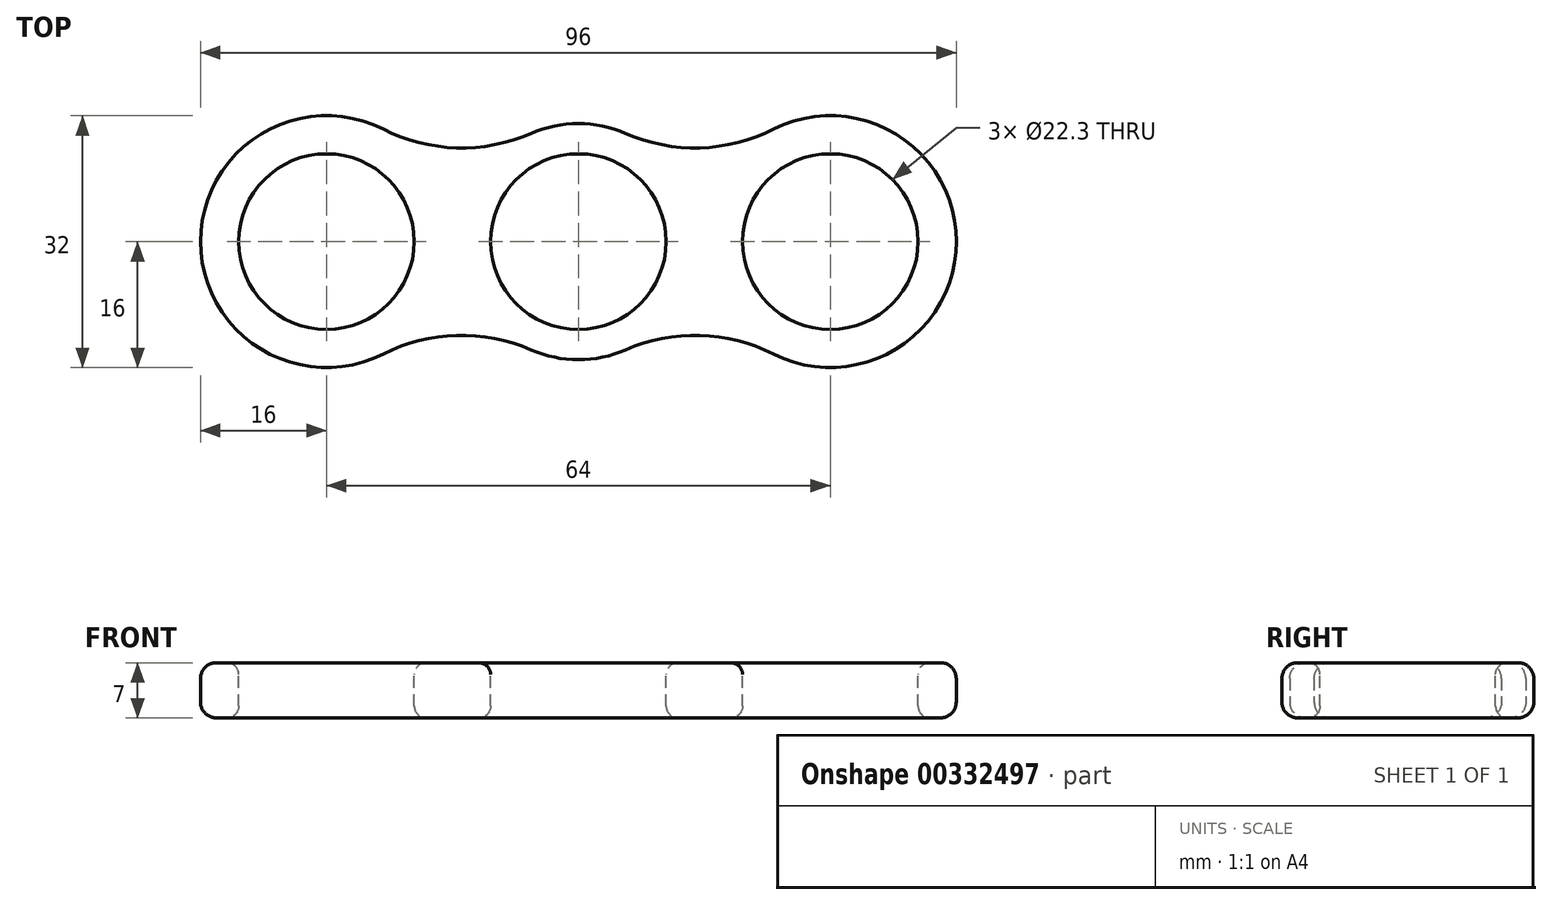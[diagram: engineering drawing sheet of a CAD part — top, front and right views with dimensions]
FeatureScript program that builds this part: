
annotation { "Feature Type Name" : "Feature", "Feature Type Description" : "" }
export const myFeature = defineFeature(function(context is Context, id is Id, definition is map)
    precondition{}
    {
        {
            var Q0;
            Q0=qCreatedBy(makeId("Top.planeOp"),FACE);
            var sketch = newSketch(context, id + "F0", { "sketchPlane" : qUnion([Q0])});
            skArc(sketch, "E0", {"start": v(-6.01, -13.74) * mm, "mid": v(0, -15) * mm, "end": v(6.01, -13.74) * mm});
            skArc(sketch, "E1", {"start": v(-24.77, 14.27) * mm, "mid": v(-45.74, 8.2) * mm, "end": v(-41.14, -13.13) * mm});
            skArc(sketch, "E2", {"start": v(24.77, -14.27) * mm, "mid": v(33.11, -15.96) * mm, "end": v(41.14, -13.13) * mm});
            skArc(sketch, "E3", {"start": v(-24.77, 14.27) * mm, "mid": v(-15.45, 11.9) * mm, "end": v(-6.01, 13.74) * mm});
            skArc(sketch, "E4", {"start": v(-6.01, -13.74) * mm, "mid": v(-15.45, -11.9) * mm, "end": v(-24.77, -14.27) * mm});
            skArc(sketch, "E5", {"start": v(6.01, 13.74) * mm, "mid": v(15.45, 11.9) * mm, "end": v(24.77, 14.27) * mm});
            skArc(sketch, "E6", {"start": v(24.77, -14.27) * mm, "mid": v(15.45, -11.9) * mm, "end": v(6.01, -13.74) * mm});
            skArc(sketch, "E7.trimOffspring", {"start": v(6.01, 13.74) * mm, "mid": v(0, 15) * mm, "end": v(-6.01, 13.74) * mm});
            skArc(sketch, "E8.trimOffspring", {"start": v(-41.14, -13.13) * mm, "mid": v(-33.11, -15.96) * mm, "end": v(-24.77, -14.27) * mm});
            skArc(sketch, "E9.trimOffspring", {"start": v(41.14, -13.13) * mm, "mid": v(45.74, 8.2) * mm, "end": v(24.77, 14.27) * mm});
            skSolve(sketch);
        }
        {
            var Q0;
            Q0 = qSketchRegion(id + "F0", true);
            extrude(context, id + "F1", {"entities" : qUnion([Q0]), "depth" : 7 * mm});
        }
        {
            var Q0;
            Q0=makeQuery(id+"F1.opExtrude","CAP_FACE",FACE,{"disambiguationData":[OSD([sQuery(id+"F0.wireOp",EDGE,"E0"),sQuery(id+"F0.wireOp",EDGE,"E1"),sQuery(id+"F0.wireOp",EDGE,"E2"),sQuery(id+"F0.wireOp",EDGE,"E3"),sQuery(id+"F0.wireOp",EDGE,"E4"),sQuery(id+"F0.wireOp",EDGE,"E5"),sQuery(id+"F0.wireOp",EDGE,"E6"),sQuery(id+"F0.wireOp",EDGE,"E7.trimOffspring")])],"isStart":false});
            var sketch = newSketch(context, id + "F2", { "sketchPlane" : qUnion([Q0])});
            skCircle(sketch, "E10", {"center": v(0, 0) * mm, "radius": 11.15 * mm});
            skPoint(sketch, "E10.perimeterSnap0", {"position": v(0, 15) * mm});
            skPoint(sketch, "E10.perimeterSnap1", {"position": v(-15.45, 11.9) * mm});
            skCircle(sketch, "E11", {"center": v(-32, 0) * mm, "radius": 11.15 * mm});
            skCircle(sketch, "E12", {"center": v(32, 0) * mm, "radius": 11.15 * mm});
            skSolve(sketch);
        }
        {
            var Q0;
            Q0 = qSketchRegion(id + "F2", true);
            extrude(context, id + "F3", {"entities" : qUnion([Q0]), "operationType" : NewBodyOperationType.REMOVE, "endBound" : BoundingType.THROUGH_ALL, "oppositeDirection" : true, "depth" : 25 * mm});
        }
        {
            var Q0;
            Q0=makeQuery(id+"F1.opExtrude","SWEPT_FACE",FACE,{"disambiguationData":[OSD([sQuery(id+"F0.wireOp",EDGE,"E1"),sQuery(id+"F0.wireOp",EDGE,"E8.trimOffspring")])]});
            var Q1;
            Q1=makeQuery(id+"F1.opExtrude","SWEPT_FACE",FACE,{"disambiguationData":[OSD([sQuery(id+"F0.wireOp",EDGE,"E4")])]});
            var Q2;
            Q2=makeQuery(id+"F1.opExtrude","SWEPT_FACE",FACE,{"disambiguationData":[OSD([sQuery(id+"F0.wireOp",EDGE,"E0")])]});
            var Q3;
            Q3=makeQuery(id+"F1.opExtrude","SWEPT_FACE",FACE,{"disambiguationData":[OSD([sQuery(id+"F0.wireOp",EDGE,"E6")])]});
            var Q4;
            Q4=makeQuery(id+"F1.opExtrude","SWEPT_FACE",FACE,{"disambiguationData":[OSD([sQuery(id+"F0.wireOp",EDGE,"E2"),sQuery(id+"F0.wireOp",EDGE,"E9.trimOffspring")])]});
            var Q5;
            Q5=makeQuery(id+"F1.opExtrude","SWEPT_FACE",FACE,{"disambiguationData":[OSD([sQuery(id+"F0.wireOp",EDGE,"E5")])]});
            var Q6;
            Q6=makeQuery(id+"F1.opExtrude","SWEPT_FACE",FACE,{"disambiguationData":[OSD([sQuery(id+"F0.wireOp",EDGE,"E7.trimOffspring")])]});
            var Q7;
            Q7=makeQuery(id+"F1.opExtrude","SWEPT_FACE",FACE,{"disambiguationData":[OSD([sQuery(id+"F0.wireOp",EDGE,"E3")])]});
            fillet(context, id + "F4", {"entities" : qUnion([Q0, Q1, Q2, Q3, Q4, Q5, Q6, Q7]), "radius" : 2 * mm, "tangentPropagation" : true, "allowEdgeOverflow" : false});
        }
        {
            var Q0;
            Q0=makeQuery(id+"F3.boolean.opBoolean","COPY",FACE,{"derivedFrom":makeQuery(id+"F3.opExtrude","SWEPT_FACE",FACE,{"disambiguationData":[OSD([sQuery(id+"F2.wireOp",EDGE,"E12")])]})});
            var Q1;
            Q1=makeQuery(id+"F3.boolean.opBoolean","COPY",FACE,{"derivedFrom":makeQuery(id+"F3.opExtrude","SWEPT_FACE",FACE,{"disambiguationData":[OSD([sQuery(id+"F2.wireOp",EDGE,"E10")])]})});
            var Q2;
            Q2=makeQuery(id+"F3.boolean.opBoolean","COPY",FACE,{"derivedFrom":makeQuery(id+"F3.opExtrude","SWEPT_FACE",FACE,{"disambiguationData":[OSD([sQuery(id+"F2.wireOp",EDGE,"E11")])]})});
            fillet(context, id + "F5", {"entities" : qUnion([Q0, Q1, Q2]), "radius" : 1.5 * mm, "tangentPropagation" : true, "allowEdgeOverflow" : false});
        }
    });
